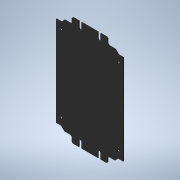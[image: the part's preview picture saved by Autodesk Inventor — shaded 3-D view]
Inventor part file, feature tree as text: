
AUTODESK INVENTOR PART (.ipt)
format: ipt  version: 2021 (Build 250183000, 183)  size: 161,280 bytes
history: native  units: mm
features: other x7, extrude x1, sketch x1
ambient origin geometry x8: Origin, YZ Plane, XZ Plane, XY Plane, X Axis, Y Axis, Z Axis, Center Point
bodies: Solid1 (feature_tree)
feature tree (9):
  extrude  "Extrusion1"  TaperAngle=0.0deg  [1 undecoded]
  other  "MONTAGEPLATTE_XY"
  other  "MONTAGEPLATTE_YZ"
  other  "MONTAGEPLATTE_ZX"
  other  "MONTAGEPLATTE_X"
  other  "MONTAGEPLATTE_Y"
  other  "MONTAGEPLATTE_Z"
  other  "MONTAGEPLATTE_Center"
  sketch  "Sketch_7"  dims[d0=2.0mm d1=0.0mm d2=0.0mm]
note: 1 required parameter value undecoded (feature->parameter linkage not recoverable at this tier; creation-order binding heuristic only, values carry confidence <= 0.55)
